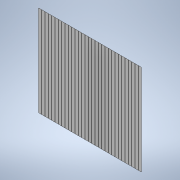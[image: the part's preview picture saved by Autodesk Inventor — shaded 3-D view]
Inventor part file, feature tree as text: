
AUTODESK INVENTOR PART (.ipt)
format: ipt  version: 2021 (Build 250183000, 183)  size: 222,720 bytes
history: native  units: in
note: dims shown in document units (in); Inventor stores cm internally (conversion verified against a paired STEP export)
features: extrude x3, sketch x3, pattern_linear x1, projected_geometry x1
ambient origin geometry x8: Origin, YZ Plane, XZ Plane, XY Plane, X Axis, Y Axis, Z Axis, Center Point
bodies: Solid1 (feature_tree)
feature tree (8):
  extrude  "Extrusion1"  Depth=3.0in
  extrude  "Extrusion2"  Depth=0.1in
  pattern_linear  "Rectangular Pattern1"  Count1=31 Spacing1=0.11in
  extrude  "Extrusion3"  Depth=1.0in TaperAngle=0.0deg
  sketch  "Sketch1"  dims[d0=4.0in d1=3.0in]
  sketch  "Sketch2"  dims[d2=0.04in d3=0.0in d4=0.1in]
  projected_geometry  "Projected Loop1"
  sketch  "Sketch3"  dims[d5=0.0015in d6=0.0in d7=12.2047in d9=0.11in d10=1.0in d11=0.0in]
